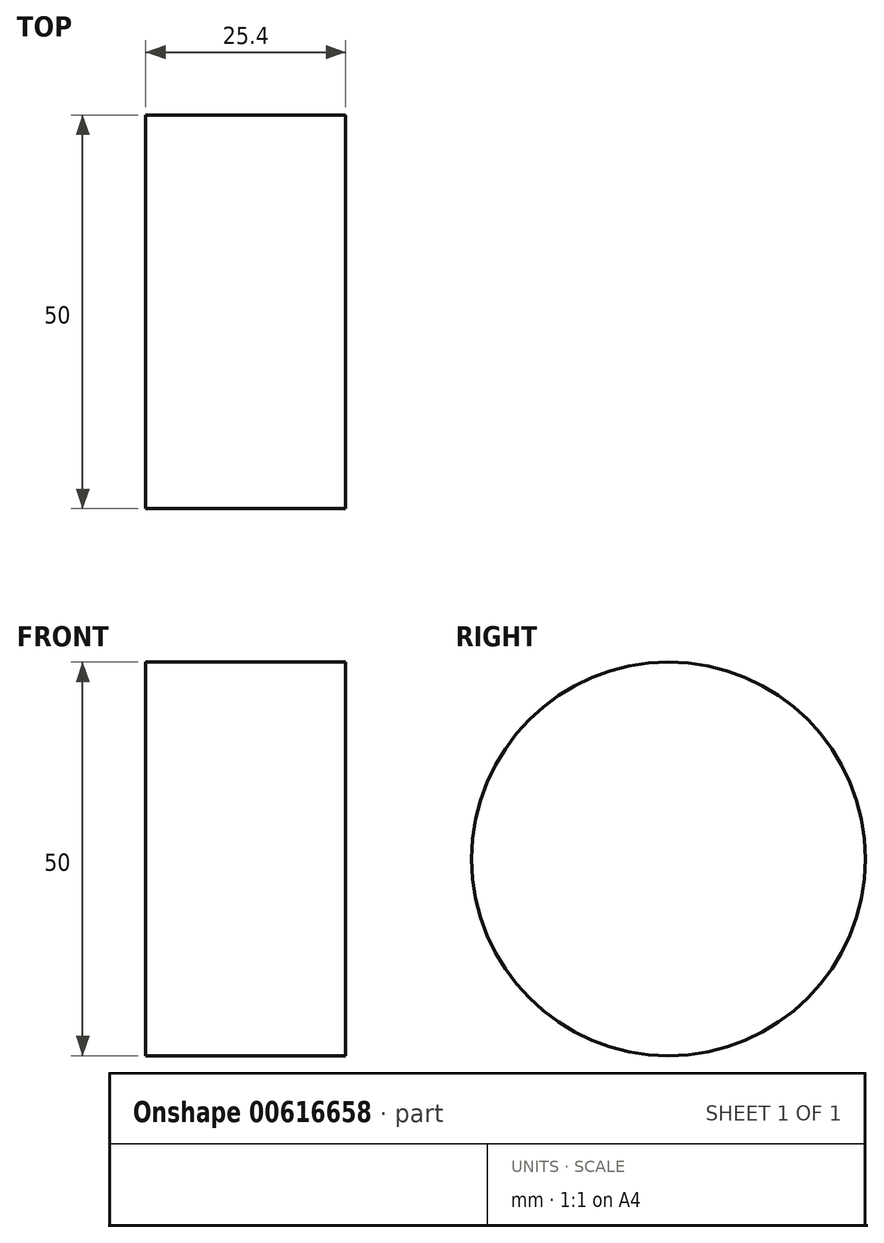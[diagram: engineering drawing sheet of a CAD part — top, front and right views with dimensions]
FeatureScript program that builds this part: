
annotation { "Feature Type Name" : "Feature", "Feature Type Description" : "" }
export const myFeature = defineFeature(function(context is Context, id is Id, definition is map)
    precondition{}
    {
        {
            var Q0;
            Q0=qCreatedBy(makeId("Right.planeOp"),FACE);
            var sketch = newSketch(context, id + "F0", { "sketchPlane" : qUnion([Q0])});
            skCircle(sketch, "E0", {"center": v(0, 0) * mm, "radius": 25 * mm});
            skSolve(sketch);
        }
        {
            var Q0;
            Q0=makeQuery(id+"F0.imprint","IMPRINT",FACE,{"disambiguationData":[TD([[makeQuery(id+"F0.imprint","IMPRINT",EDGE,{"derivedFrom":sQuery(id+"F0.wireOp",EDGE,"E0")}),1.0]])]});
            extrude(context, id + "F1", {"entities" : qUnion([Q0]), "depth" : 25.4 * mm, "offsetDistance" : 25.4 * mm});
        }
    });
